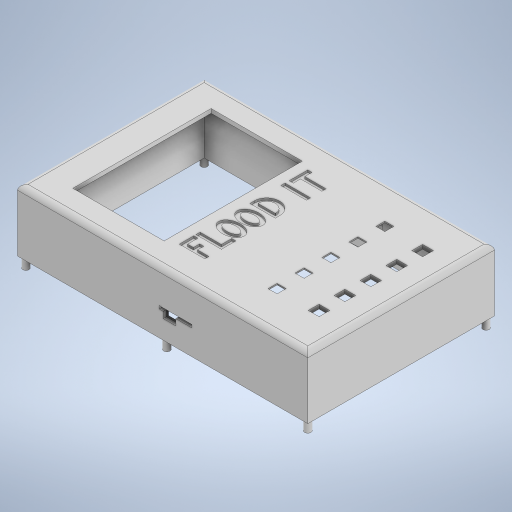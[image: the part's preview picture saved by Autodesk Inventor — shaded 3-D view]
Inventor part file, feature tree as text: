
AUTODESK INVENTOR PART (.ipt)
format: ipt  version: 2023 (Build 270158000, 158)  size: 638,976 bytes
history: native  units: in
note: dims shown in document units (in); Inventor stores cm internally (conversion verified against a paired STEP export)
features: extrude x14, sketch x12, fillet x1
ambient origin geometry x8: Origin, YZ Plane, XZ Plane, XY Plane, X Axis, Y Axis, Z Axis, Center Point
bodies: Solid1 (feature_tree)
feature tree (27):
  extrude  "Extrusion1"  Depth=7.0in
  extrude  "Extrusion2"  Depth=1.4in
  fillet  "Fillet1"  Radius=1.4in
  extrude  "Extrusion3"  Depth=0.25in
  extrude  "Extrusion4"  Depth=2.2in
  extrude  "Extrusion5"  Depth=0.5825in
  sketch  "Sketch6"  dims[d13=0.75in d14=1.4in d15=0.0in]
  extrude  "Extrusion9"  Depth=1.4in TaperAngle=0.0deg
  extrude  "Extrusion10"  Depth=0.1in
  extrude  "Extrusion11"  Depth=0.1in
  extrude  "Extrusion12"  Depth=0.25in
  extrude  "Extrusion13"  Depth=0.15in
  extrude  "Extrusion14"  Depth=0.7in
  extrude  "Extrusion15"  Depth=0.1in
  extrude  "Extrusion19"  Depth=0.625in
  extrude  "Extrusion21"  Depth=0.625in
  sketch  "Sketch1"  dims[d0=7.0in d1=4.5in]
  sketch  "Sketch2"  dims[d2=1.5in d3=0.0in d4=0.2in d5=1.4in d6=0.0in]
  sketch  "Sketch3"  dims[d7=0.125in d8=0.25in]
  sketch  "Sketch4"  dims[d9=0.25in d10=2.2in]
  sketch  "Sketch5"  dims[d11=3.335in d12=0.5825in]
  sketch  "Sketch8"  dims[d16=0.1in d17=0.14in]
  sketch  "Sketch9"  dims[d18=0.1in d19=0.275in]
  sketch  "Sketch10"  dims[d20=0.35in d21=0.25in]
  sketch  "Sketch11"  dims[d22=0.15in d23=0.15in]
  sketch  "Sketch12"  dims[d24=0.25in d25=0.7in]
  sketch  "Sketch16"  dims[d26=0.1in d27=0.1in d28=0.25in d29=0.615in d30=0.25in d31=1.1in d32=0.21in d33=0.3075in d34=0.5575in d35=1.65in d36=0.3075in d37=0.21in d38=0.5575in d39=2.1in d40=0.1in d41=0.1in d42=0.3in d43=0.1in d44=0.25in d45=0.615in d46=2.4in d47=0.11in d48=2.51in d49=0.5575in d50=0.1in d51=0.615in d52=0.175in d53=0.175in d54=0.1in d55=0.1in d56=0.25in d57=3.15in d58=0.1in d59=0.515in d60=0.05in d61=0.0in d62=0.1175in d63=0.1175in d64=0.2175in d65=0.2175in d66=0.2175in d67=0.2175in d68=0.2175in d69=0.2175in d70=0.65in d71=0.65in d72=0.65in d73=0.65in d74=0.8413in d76=2.25in d92=1.0in d93=0.0in d124=0.0688in d125=0.0in d126=0.25in d127=0.275in d128=0.25in d129=0.25in d130=0.25in d131=2.1in d132=0.2in d134=0.05in d135=0.0in d142=0.0375in d143=0.0in d144=2.0in d145=0.785in d146=0.0725in d147=0.3in d148=0.15in d149=0.1in d150=0.7in d151=0.2in d152=0.0in d153=0.075in d154=0.125in d155=0.0in d156=0.285in d157=2.5in d158=0.49in d159=0.25in d160=0.0in d161=0.49in d162=0.081in d163=0.0in d164=0.45in d187=2.8in d189=0.04in d190=0.04in d191=0.04in d192=0.04in d193=0.04in d194=0.485in d195=0.0938in d197=3.325in d198=0.254in d199=0.1735in d219=0.285in d220=0.1425in d221=0.245in d222=0.285in d224=0.8413in d225=0.15in d226=0.15in d227=0.15in d228=0.15in d229=0.15in d230=0.15in d231=0.1in d232=0.1in d233=0.1in d234=0.1in d235=0.1in d236=0.1in d237=0.1in d238=0.1in d239=0.1in d240=0.1in d241=3.5in d242=3.5in d243=0.245in d244=0.0in d245=0.0625in d248=0.26in d249=0.26in d250=1.9685in d252=0.625in d253=0.3937in d255=1.0in d257=0.67in d258=0.67in d259=0.4in d260=1.0in d261=0.0in]
